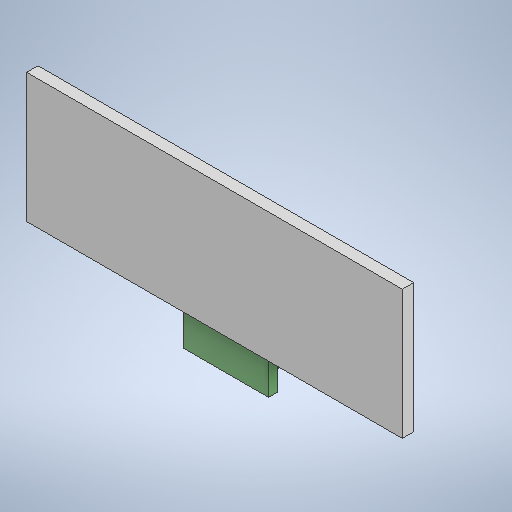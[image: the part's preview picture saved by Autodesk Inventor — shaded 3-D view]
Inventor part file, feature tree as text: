
AUTODESK INVENTOR PART (.ipt)
format: ipt  version: 2025.3 (Build 293356000, 356)  size: 239,616 bytes
history: native  units: mm
features: extrude x3, sketch x3, other x1
ambient origin geometry x8: Origin, YZ Plane, XZ Plane, XY Plane, X Axis, Y Axis, Z Axis, Center Point
bodies: Body1 (feature_tree)
feature tree (7):
  other  "ソリッド1"
  extrude  "押し出し1"  Depth=66.0mm
  extrude  "押し出し2"  Depth=22.7mm
  extrude  "押し出し3"  Depth=2.0mm TaperAngle=0.0deg
  sketch  "スケッチ1"
  sketch  "スケッチ3"
  sketch  "スケッチ4"
